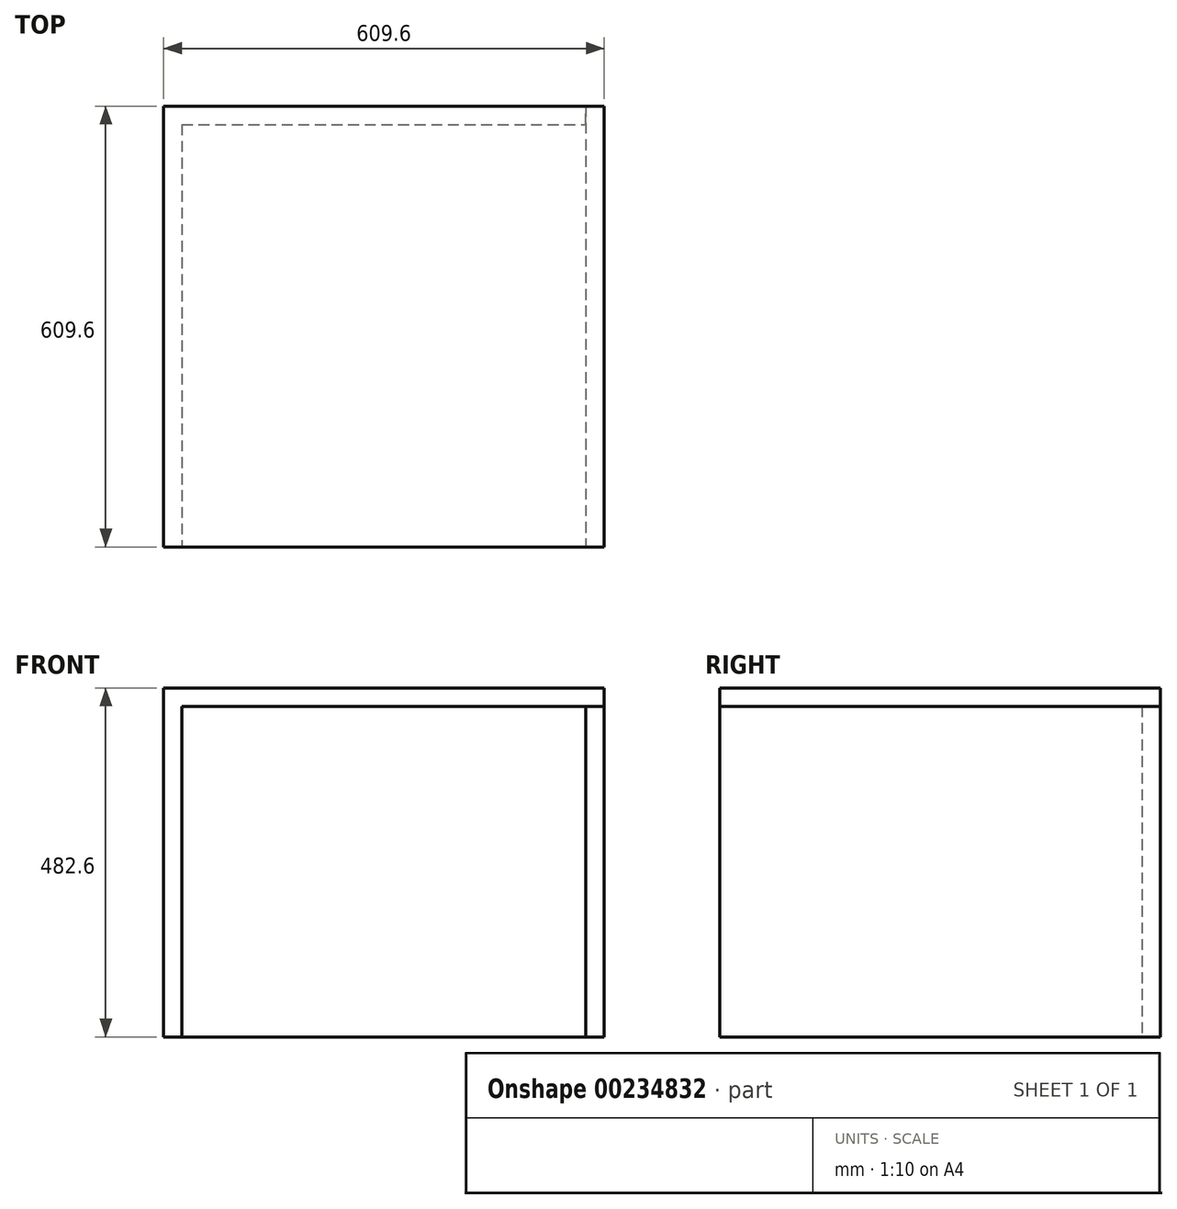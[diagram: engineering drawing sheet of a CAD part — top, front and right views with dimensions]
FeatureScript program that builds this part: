
annotation { "Feature Type Name" : "Feature", "Feature Type Description" : "" }
export const myFeature = defineFeature(function(context is Context, id is Id, definition is map)
    precondition{}
    {
        {
            var Q0;
            Q0=qCreatedBy(makeId("Top.planeOp"),FACE);
            var sketch = newSketch(context, id + "F0", { "sketchPlane" : qUnion([Q0])});
            skLineSegment(sketch, "E0.bottom", {"start": v(0, 0) * mm, "end": v(609.6, 0) * mm});
            skLineSegment(sketch, "E0.top", {"start": v(0, -609.6) * mm, "end": v(609.6, -609.6) * mm});
            skLineSegment(sketch, "E0.left", {"start": v(0, 0) * mm, "end": v(0, -609.6) * mm});
            skLineSegment(sketch, "E0.right", {"start": v(609.6, 0) * mm, "end": v(609.6, -609.6) * mm});
            skSolve(sketch);
        }
        {
            var Q0;
            Q0=makeQuery(id+"F0.imprint","IMPRINT",FACE,{"disambiguationData":[TD([[makeQuery(id+"F0.imprint","IMPRINT",EDGE,{"derivedFrom":sQuery(id+"F0.wireOp",EDGE,"E0.bottom")}),-1.0]])]});
            extrude(context, id + "F1", {"entities" : qUnion([Q0]), "depth" : 25.4 * mm});
        }
        {
            var Q0;
            Q0=makeQuery(id+"F1.opExtrude","SWEPT_FACE",FACE,{"disambiguationData":[OSD([sQuery(id+"F0.wireOp",EDGE,"E0.right")])]});
            var sketch = newSketch(context, id + "F2", { "sketchPlane" : qUnion([Q0])});
            skLineSegment(sketch, "E1.bottom", {"start": v(0, 0) * mm, "end": v(-609.6, 0) * mm});
            skLineSegment(sketch, "E1.top", {"start": v(0, -457.2) * mm, "end": v(-609.6, -457.2) * mm});
            skLineSegment(sketch, "E1.left", {"start": v(0, 0) * mm, "end": v(0, -457.2) * mm});
            skLineSegment(sketch, "E1.right", {"start": v(-609.6, 0) * mm, "end": v(-609.6, -457.2) * mm});
            skSolve(sketch);
        }
        {
            var Q0;
            Q0=makeQuery(id+"F2.imprint","IMPRINT",FACE,{"disambiguationData":[TD([[makeQuery(id+"F2.imprint","IMPRINT",EDGE,{"derivedFrom":sQuery(id+"F2.wireOp",EDGE,"E1.bottom")}),1.0]])]});
            extrude(context, id + "F3", {"entities" : qUnion([Q0]), "oppositeDirection" : true, "depth" : 25.4 * mm});
        }
        {
            var Q0;
            Q0=makeQuery(id+"F1.opExtrude","SWEPT_FACE",FACE,{"disambiguationData":[OSD([sQuery(id+"F0.wireOp",EDGE,"E0.left")])]});
            var sketch = newSketch(context, id + "F4", { "sketchPlane" : qUnion([Q0])});
            skLineSegment(sketch, "E2.bottom", {"start": v(0, 0) * mm, "end": v(609.6, 0) * mm});
            skLineSegment(sketch, "E2.top", {"start": v(0, -457.2) * mm, "end": v(609.6, -457.2) * mm});
            skLineSegment(sketch, "E2.left", {"start": v(0, 0) * mm, "end": v(0, -457.2) * mm});
            skLineSegment(sketch, "E2.right", {"start": v(609.6, 0) * mm, "end": v(609.6, -457.2) * mm});
            skSolve(sketch);
        }
        {
            var Q0;
            Q0=makeQuery(id+"F4.imprint","IMPRINT",FACE,{"disambiguationData":[TD([[makeQuery(id+"F4.imprint","IMPRINT",EDGE,{"derivedFrom":sQuery(id+"F4.wireOp",EDGE,"E2.bottom")}),-1.0]])]});
            extrude(context, id + "F5", {"entities" : qUnion([Q0]), "oppositeDirection" : true, "depth" : 25.4 * mm});
        }
        {
            var Q0;
            Q0=makeQuery(id+"F1.opExtrude","SWEPT_FACE",FACE,{"disambiguationData":[OSD([sQuery(id+"F0.wireOp",EDGE,"E0.bottom")])]});
            var sketch = newSketch(context, id + "F6", { "sketchPlane" : qUnion([Q0])});
            skLineSegment(sketch, "E3.bottom", {"start": v(-584.14, 0) * mm, "end": v(-25.34, 0) * mm});
            skLineSegment(sketch, "E3.top", {"start": v(-584.14, -457.2) * mm, "end": v(-25.34, -457.2) * mm});
            skLineSegment(sketch, "E3.left", {"start": v(-584.14, 0) * mm, "end": v(-584.14, -457.2) * mm});
            skLineSegment(sketch, "E3.right", {"start": v(-25.34, 0) * mm, "end": v(-25.34, -457.2) * mm});
            skSolve(sketch);
        }
        {
            var Q0;
            Q0=makeQuery(id+"F6.imprint","IMPRINT",FACE,{"disambiguationData":[TD([[makeQuery(id+"F6.imprint","IMPRINT",EDGE,{"derivedFrom":sQuery(id+"F6.wireOp",EDGE,"E3.bottom")}),1.0]])]});
            extrude(context, id + "F7", {"entities" : qUnion([Q0]), "operationType" : NewBodyOperationType.ADD, "oppositeDirection" : true, "depth" : 25.4 * mm});
        }
    });
